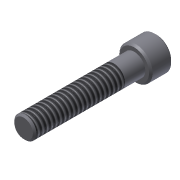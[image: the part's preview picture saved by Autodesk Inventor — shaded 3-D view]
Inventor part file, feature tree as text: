
AUTODESK INVENTOR PART (.ipt)
format: ipt  version: 2011 (Build 150239000, 239)  size: 107,008 bytes
history: native  units: in
note: dims shown in document units (in); Inventor stores cm internally (conversion verified against a paired STEP export)
features: extrude x3, sketch x3, chamfer x1, thread x1
ambient origin geometry x8: Origin, YZ Plane, XZ Plane, XY Plane, X Axis, Y Axis, Z Axis, Center Point
bodies: Solid1 (feature_tree)
feature tree (8):
  extrude  "Extrusion1"  Depth=1.25in TaperAngle=0.0deg
  extrude  "Extrusion2"  Depth=0.25in TaperAngle=0.0deg
  extrude  "Extrusion3"  Depth=0.125in TaperAngle=0.0deg
  chamfer  "Chamfer1"  Distance=0.02in Angle=45.0deg
  thread  "Thread1"  [1 undecoded]
  sketch  "Sketch1"  dims[d0=0.25in d1=1.25in d2=0.0in]
  sketch  "Sketch2"  dims[d3=0.375in d4=0.25in d5=0.0in]
  sketch  "Sketch3"  dims[d6=0.1875in d7=0.125in d8=0.0in d9=0.02in d10=0.125in d11=45.0deg d12=1.0in d13=0.0in]
note: 1 required parameter value undecoded (feature->parameter linkage not recoverable at this tier; creation-order binding heuristic only, values carry confidence <= 0.55)
